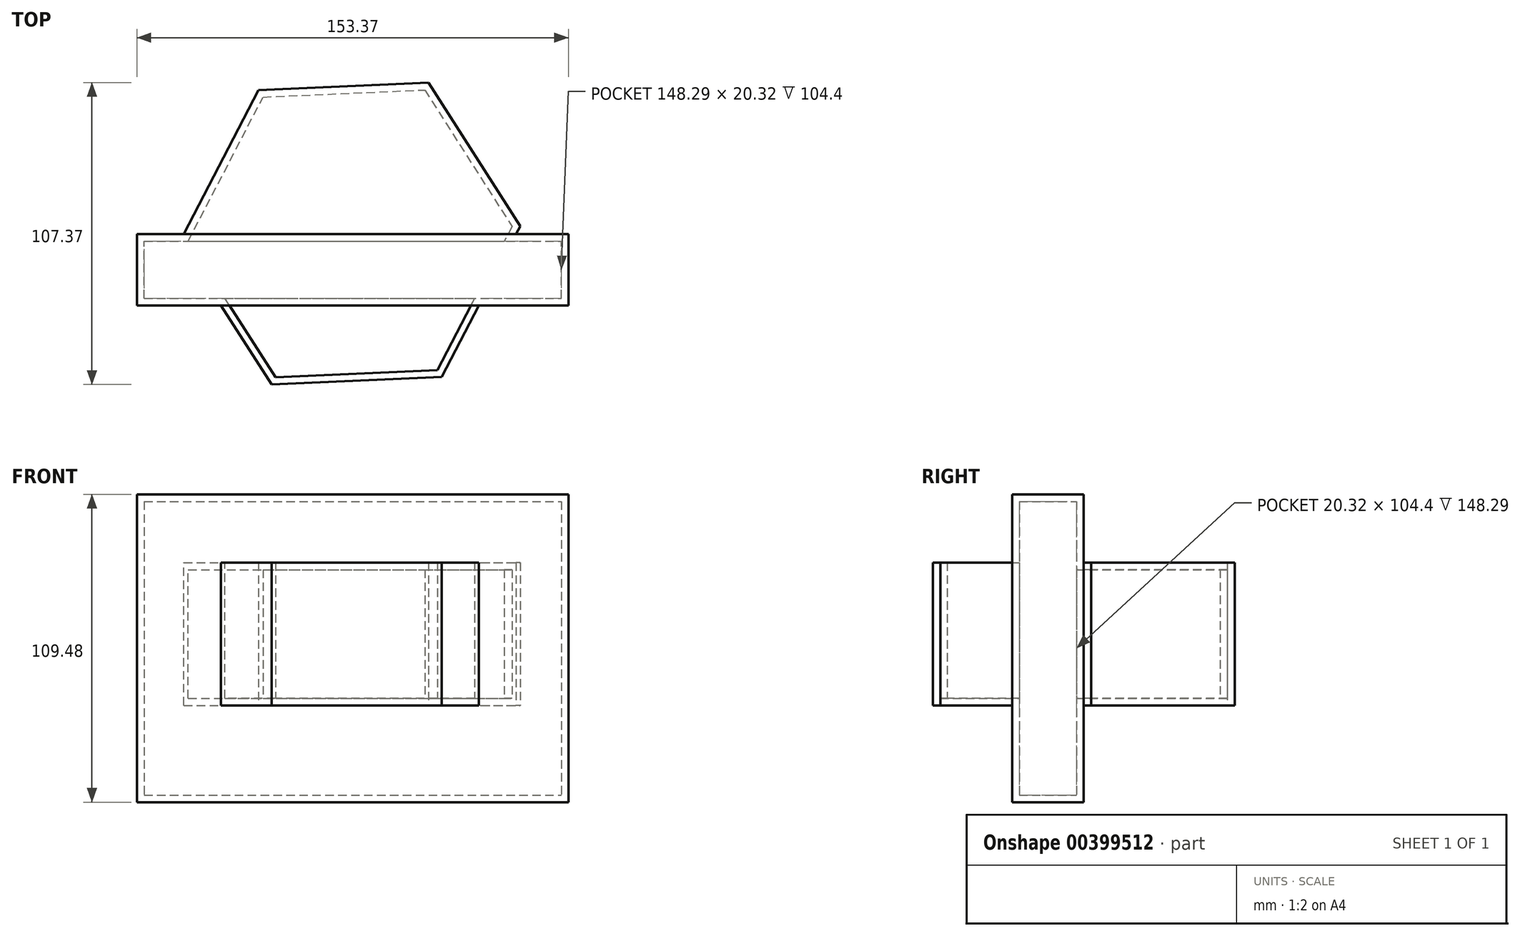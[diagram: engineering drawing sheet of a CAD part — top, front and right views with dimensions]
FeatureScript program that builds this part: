
annotation { "Feature Type Name" : "Feature", "Feature Type Description" : "" }
export const myFeature = defineFeature(function(context is Context, id is Id, definition is map)
    precondition{}
    {
        {
            var Q0;
            Q0=qCreatedBy(makeId("Top.planeOp"),FACE);
            var sketch = newSketch(context, id + "F0", { "sketchPlane" : qUnion([Q0])});
            skCircle(sketch, "E0.cCircle", {"center": v(0, 0.1) * mm, "radius": 52.4 * mm, "construction": true});
            skLineSegment(sketch, "E0.0", {"start": v(60.45, 2.77) * mm, "end": v(32.54, -50.92) * mm});
            skLineSegment(sketch, "E0.1", {"start": v(32.54, -50.92) * mm, "end": v(-27.9, -53.6) * mm});
            skLineSegment(sketch, "E0.2", {"start": v(-27.9, -53.6) * mm, "end": v(-60.45, -2.58) * mm});
            skLineSegment(sketch, "E0.3", {"start": v(-60.45, -2.58) * mm, "end": v(-32.54, 51.1) * mm});
            skLineSegment(sketch, "E0.4", {"start": v(-32.54, 51.1) * mm, "end": v(27.9, 53.78) * mm});
            skLineSegment(sketch, "E0.5", {"start": v(27.9, 53.78) * mm, "end": v(60.45, 2.77) * mm});
            skPoint(sketch, "E0.0.midPoint", {"position": v(46.5, -24.07) * mm});
            skSolve(sketch);
        }
        {
            var Q0;
            Q0=makeQuery(id+"F0.imprint","IMPRINT",FACE,{"disambiguationData":[TD([[makeQuery(id+"F0.imprint","IMPRINT",EDGE,{"derivedFrom":sQuery(id+"F0.wireOp",EDGE,"E0.0")}),-1.0]])]});
            extrude(context, id + "F1", {"entities" : qUnion([Q0]), "depth" : 50.8 * mm});
        }
        {
            var Q0;
            Q0=qCreatedBy(makeId("Front.planeOp"),FACE);
            var sketch = newSketch(context, id + "F2", { "sketchPlane" : qUnion([Q0])});
            skLineSegment(sketch, "E1.bottom", {"start": v(-75.77, 75.06) * mm, "end": v(77.6, 75.06) * mm});
            skLineSegment(sketch, "E1.top", {"start": v(-75.77, -34.42) * mm, "end": v(77.6, -34.42) * mm});
            skLineSegment(sketch, "E1.left", {"start": v(-75.77, 75.06) * mm, "end": v(-75.77, -34.42) * mm});
            skLineSegment(sketch, "E1.right", {"start": v(77.6, 75.06) * mm, "end": v(77.6, -34.42) * mm});
            skSolve(sketch);
        }
        {
            var Q0;
            Q0=makeQuery(id+"F2.imprint","IMPRINT",FACE,{"disambiguationData":[TD([[makeQuery(id+"F2.imprint","IMPRINT",EDGE,{"derivedFrom":sQuery(id+"F2.wireOp",EDGE,"E1.bottom")}),-1.0]])]});
            extrude(context, id + "F3", {"entities" : qUnion([Q0]), "operationType" : NewBodyOperationType.ADD, "depth" : 25.4 * mm});
        }
        {
            var Q0;
            {var subQ0=sQuery(id+"F0.wireOp",EDGE,"E0.0");var subQ1=sQuery(id+"F0.wireOp",EDGE,"E0.1");var subQ2=sQuery(id+"F0.wireOp",EDGE,"E0.2");Q0=makeQuery(id+"F3.boolean.opBoolean","SPLIT",FACE,{"disambiguationData":[TD([makeQuery(id+"F1.opExtrude","SWEPT_FACE",FACE,{"disambiguationData":[OSD([subQ1])]})])],"derivedFrom":makeQuery(id+"F1.opExtrude","CAP_FACE",FACE,{"disambiguationData":[OSD([subQ0,subQ1,subQ2,sQuery(id+"F0.wireOp",EDGE,"E0.3"),sQuery(id+"F0.wireOp",EDGE,"E0.4"),sQuery(id+"F0.wireOp",EDGE,"E0.5")])],"isStart":false})});}
            shell(context, id + "F4", {"entities" : qUnion([Q0]), "thickness" : 2.54 * mm});
        }
    });
